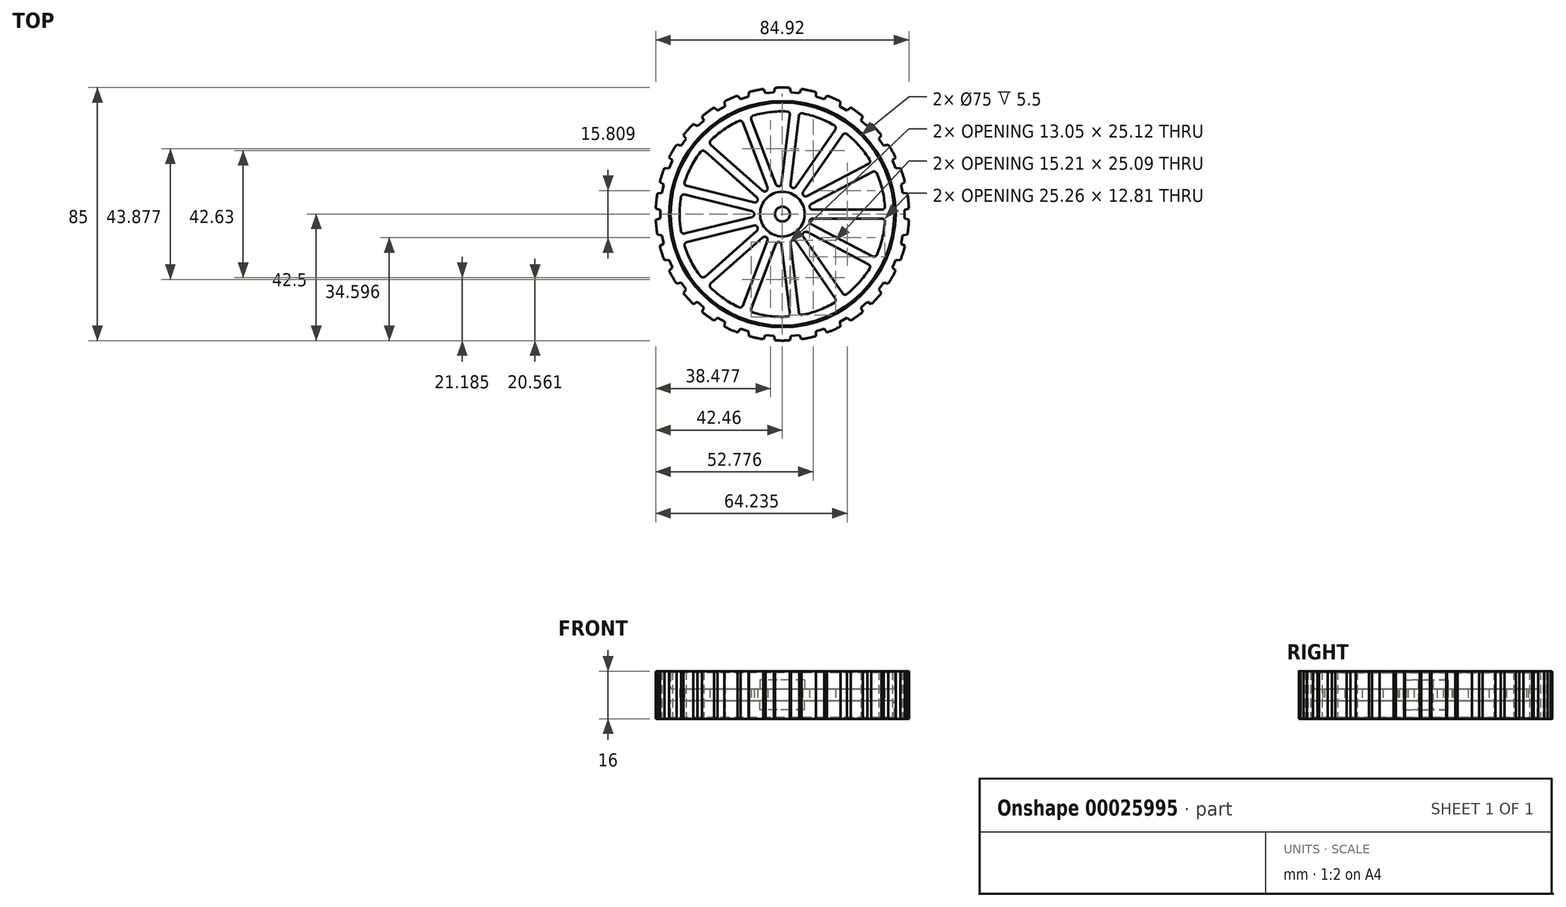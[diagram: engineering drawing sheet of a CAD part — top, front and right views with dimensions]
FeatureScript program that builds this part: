
annotation { "Feature Type Name" : "Feature", "Feature Type Description" : "" }
export const myFeature = defineFeature(function(context is Context, id is Id, definition is map)
    precondition{}
    {
        {
            var Q0;
            Q0=qCreatedBy(makeId("Top.planeOp"),FACE);
            var sketch = newSketch(context, id + "F0", { "sketchPlane" : qUnion([Q0])});
            skCircle(sketch, "E0.0", {"center": v(0, 0) * mm, "radius": 37.5 * mm});
            skCircle(sketch, "E1", {"center": v(0, 0) * mm, "radius": 2.5 * mm});
            skCircle(sketch, "E2.0", {"center": v(0, 0) * mm, "radius": 6.27 * mm, "construction": true});
            skLineSegment(sketch, "E3", {"start": v(-10.2, 0.97) * mm, "end": v(-32.8, 6.54) * mm});
            skLineSegment(sketch, "E4", {"start": v(-33.82, -6.8) * mm, "end": v(-33.82, -6.8) * mm});
            skLineSegment(sketch, "E5", {"start": v(0, 0) * mm, "end": v(-42.5, 0) * mm, "construction": true});
            skPoint(sketch, "E6.visualSharp", {"position": v(-6.27, 0) * mm});
            skArc(sketch, "E6.filletArc", {"start": v(-10.2, -0.97) * mm, "mid": v(-9.45, 0) * mm, "end": v(-10.2, 0.97) * mm});
            skLineSegment(sketch, "E7", {"start": v(-33.82, 6.8) * mm, "end": v(-33.82, 6.8) * mm});
            skLineSegment(sketch, "E8", {"start": v(-33.82, -6.8) * mm, "end": v(-32.8, -6.54) * mm, "construction": true});
            skCircle(sketch, "E9", {"center": v(0, 0) * mm, "radius": 7.5 * mm});
            skArc(sketch, "E10", {"start": v(-33.82, 6.8) * mm, "mid": v(-33.93, 6.26) * mm, "end": v(-34.02, 5.73) * mm, "construction": true});
            skLineSegment(sketch, "E11", {"start": v(-32.8, -6.54) * mm, "end": v(-10.2, -0.97) * mm});
            skArc(sketch, "E12", {"start": v(-34.02, -5.73) * mm, "mid": v(-33.93, -6.26) * mm, "end": v(-33.82, -6.8) * mm, "construction": true});
            skArc(sketch, "E13", {"start": v(-34.02, -5.73) * mm, "mid": v(-33.58, -6.4) * mm, "end": v(-32.8, -6.54) * mm});
            skArc(sketch, "E14", {"start": v(-32.8, -6.54) * mm, "mid": v(-32.49, -4.73) * mm, "end": v(-34.02, -5.73) * mm, "construction": true});
            skLineSegment(sketch, "E15", {"start": v(-32.8, 6.54) * mm, "end": v(-33.82, 6.8) * mm, "construction": true});
            skArc(sketch, "E16", {"start": v(-34.02, 5.73) * mm, "mid": v(-32.49, 4.73) * mm, "end": v(-32.8, 6.54) * mm, "construction": true});
            skArc(sketch, "E17", {"start": v(-32.8, 6.54) * mm, "mid": v(-33.58, 6.4) * mm, "end": v(-34.02, 5.73) * mm});
            skArc(sketch, "E18", {"start": v(-34.02, 5.73) * mm, "mid": v(-34.5, 0) * mm, "end": v(-34.02, -5.73) * mm});
            skLineSegment(sketch, "E19.1.0", {"start": v(-9.49, -3.88) * mm, "end": v(-32.08, -9.45) * mm});
            skArc(sketch, "E19.1.1", {"start": v(-32.08, -9.45) * mm, "mid": v(-32.71, -9.94) * mm, "end": v(-32.79, -10.73) * mm});
            skArc(sketch, "E19.1.2", {"start": v(-32.79, -10.73) * mm, "mid": v(-30.55, -16.03) * mm, "end": v(-27.46, -20.89) * mm});
            skArc(sketch, "E19.1.3", {"start": v(-27.46, -20.89) * mm, "mid": v(-26.76, -21.28) * mm, "end": v(-26, -21.03) * mm});
            skLineSegment(sketch, "E19.1.4", {"start": v(-26, -21.03) * mm, "end": v(-8.59, -5.6) * mm});
            skArc(sketch, "E19.1.5", {"start": v(-8.59, -5.6) * mm, "mid": v(-8.36, -4.39) * mm, "end": v(-9.49, -3.88) * mm});
            skLineSegment(sketch, "E19.2.0", {"start": v(-6.6, -7.85) * mm, "end": v(-24.01, -23.28) * mm});
            skArc(sketch, "E19.2.1", {"start": v(-24.01, -23.28) * mm, "mid": v(-24.35, -24) * mm, "end": v(-24.04, -24.74) * mm});
            skArc(sketch, "E19.2.2", {"start": v(-24.04, -24.74) * mm, "mid": v(-19.6, -28.4) * mm, "end": v(-14.6, -31.26) * mm});
            skArc(sketch, "E19.2.3", {"start": v(-14.6, -31.26) * mm, "mid": v(-13.8, -31.28) * mm, "end": v(-13.25, -30.7) * mm});
            skLineSegment(sketch, "E19.2.4", {"start": v(-13.25, -30.7) * mm, "end": v(-5, -8.95) * mm});
            skArc(sketch, "E19.2.5", {"start": v(-5, -8.95) * mm, "mid": v(-5.37, -7.77) * mm, "end": v(-6.6, -7.85) * mm});
            skLineSegment(sketch, "E20.2.3.0", {"start": v(-2.2, -10.02) * mm, "end": v(-10.44, -31.77) * mm});
            skArc(sketch, "E20.3.3.0", {"start": v(-10.44, -31.77) * mm, "mid": v(-10.4, -32.57) * mm, "end": v(-9.8, -33.08) * mm});
            skArc(sketch, "E20.7.3.0", {"start": v(-9.8, -33.08) * mm, "mid": v(-4.16, -34.25) * mm, "end": v(1.6, -34.46) * mm});
            skArc(sketch, "E20.11.3.0", {"start": v(1.6, -34.46) * mm, "mid": v(2.3, -34.11) * mm, "end": v(2.54, -33.34) * mm});
            skLineSegment(sketch, "E20.15.3.0", {"start": v(2.54, -33.34) * mm, "end": v(-0.27, -10.25) * mm});
            skArc(sketch, "E20.18.3.0", {"start": v(-0.27, -10.25) * mm, "mid": v(-1.14, -9.38) * mm, "end": v(-2.2, -10.02) * mm});
            skLineSegment(sketch, "E20.2.4.0", {"start": v(2.71, -9.89) * mm, "end": v(5.52, -32.98) * mm});
            skArc(sketch, "E20.3.4.0", {"start": v(5.52, -32.98) * mm, "mid": v(5.92, -33.67) * mm, "end": v(6.7, -33.84) * mm});
            skArc(sketch, "E20.7.4.0", {"start": v(6.7, -33.84) * mm, "mid": v(12.23, -32.26) * mm, "end": v(17.42, -29.78) * mm});
            skArc(sketch, "E20.11.4.0", {"start": v(17.42, -29.78) * mm, "mid": v(17.9, -29.13) * mm, "end": v(17.74, -28.35) * mm});
            skLineSegment(sketch, "E20.15.4.0", {"start": v(17.74, -28.35) * mm, "end": v(4.53, -9.2) * mm});
            skArc(sketch, "E20.18.4.0", {"start": v(4.53, -9.2) * mm, "mid": v(3.35, -8.83) * mm, "end": v(2.71, -9.89) * mm});
            skLineSegment(sketch, "E20.2.5.0", {"start": v(7, -7.5) * mm, "end": v(20.21, -26.64) * mm});
            skArc(sketch, "E20.3.5.0", {"start": v(20.21, -26.64) * mm, "mid": v(20.9, -27.06) * mm, "end": v(21.66, -26.85) * mm});
            skArc(sketch, "E20.7.5.0", {"start": v(21.66, -26.85) * mm, "mid": v(25.82, -22.88) * mm, "end": v(29.27, -18.27) * mm});
            skArc(sketch, "E20.11.5.0", {"start": v(29.27, -18.27) * mm, "mid": v(29.38, -17.48) * mm, "end": v(28.88, -16.85) * mm});
            skLineSegment(sketch, "E20.15.5.0", {"start": v(28.88, -16.85) * mm, "end": v(8.28, -6.04) * mm});
            skArc(sketch, "E20.18.5.0", {"start": v(8.28, -6.04) * mm, "mid": v(7.07, -6.26) * mm, "end": v(7, -7.5) * mm});
            skLineSegment(sketch, "E20.2.6.0", {"start": v(9.68, -3.39) * mm, "end": v(30.28, -14.2) * mm});
            skArc(sketch, "E20.3.6.0", {"start": v(30.28, -14.2) * mm, "mid": v(31.07, -14.25) * mm, "end": v(31.66, -13.7) * mm});
            skArc(sketch, "E20.7.6.0", {"start": v(31.66, -13.7) * mm, "mid": v(33.5, -8.26) * mm, "end": v(34.4, -2.57) * mm});
            skArc(sketch, "E20.11.6.0", {"start": v(34.4, -2.57) * mm, "mid": v(34.14, -1.82) * mm, "end": v(33.4, -1.5) * mm});
            skLineSegment(sketch, "E20.15.6.0", {"start": v(33.4, -1.5) * mm, "end": v(10.14, -1.5) * mm});
            skArc(sketch, "E20.18.6.0", {"start": v(10.14, -1.5) * mm, "mid": v(9.17, -2.26) * mm, "end": v(9.68, -3.39) * mm});
            skLineSegment(sketch, "E20.2.7.0", {"start": v(10.14, 1.5) * mm, "end": v(33.4, 1.5) * mm});
            skArc(sketch, "E20.3.7.0", {"start": v(33.4, 1.5) * mm, "mid": v(34.14, 1.82) * mm, "end": v(34.4, 2.57) * mm});
            skArc(sketch, "E20.7.7.0", {"start": v(34.4, 2.57) * mm, "mid": v(33.5, 8.26) * mm, "end": v(31.66, 13.7) * mm});
            skArc(sketch, "E20.11.7.0", {"start": v(31.66, 13.7) * mm, "mid": v(31.07, 14.25) * mm, "end": v(30.28, 14.2) * mm});
            skLineSegment(sketch, "E20.15.7.0", {"start": v(30.28, 14.2) * mm, "end": v(9.68, 3.39) * mm});
            skArc(sketch, "E20.18.7.0", {"start": v(9.68, 3.39) * mm, "mid": v(9.17, 2.26) * mm, "end": v(10.14, 1.5) * mm});
            skLineSegment(sketch, "E20.2.8.0", {"start": v(8.28, 6.04) * mm, "end": v(28.88, 16.85) * mm});
            skArc(sketch, "E20.3.8.0", {"start": v(28.88, 16.85) * mm, "mid": v(29.38, 17.48) * mm, "end": v(29.27, 18.27) * mm});
            skArc(sketch, "E20.7.8.0", {"start": v(29.27, 18.27) * mm, "mid": v(25.82, 22.88) * mm, "end": v(21.66, 26.85) * mm});
            skArc(sketch, "E20.11.8.0", {"start": v(21.66, 26.85) * mm, "mid": v(20.9, 27.06) * mm, "end": v(20.21, 26.64) * mm});
            skLineSegment(sketch, "E20.15.8.0", {"start": v(20.21, 26.64) * mm, "end": v(7, 7.5) * mm});
            skArc(sketch, "E20.18.8.0", {"start": v(7, 7.5) * mm, "mid": v(7.07, 6.26) * mm, "end": v(8.28, 6.04) * mm});
            skLineSegment(sketch, "E20.2.9.0", {"start": v(4.53, 9.2) * mm, "end": v(17.74, 28.35) * mm});
            skArc(sketch, "E20.3.9.0", {"start": v(17.74, 28.35) * mm, "mid": v(17.9, 29.13) * mm, "end": v(17.42, 29.78) * mm});
            skArc(sketch, "E20.7.9.0", {"start": v(17.42, 29.78) * mm, "mid": v(12.23, 32.26) * mm, "end": v(6.7, 33.84) * mm});
            skArc(sketch, "E20.11.9.0", {"start": v(6.7, 33.84) * mm, "mid": v(5.92, 33.67) * mm, "end": v(5.52, 32.98) * mm});
            skLineSegment(sketch, "E20.15.9.0", {"start": v(5.52, 32.98) * mm, "end": v(2.71, 9.89) * mm});
            skArc(sketch, "E20.18.9.0", {"start": v(2.71, 9.89) * mm, "mid": v(3.35, 8.83) * mm, "end": v(4.53, 9.2) * mm});
            skLineSegment(sketch, "E21.2.10.0", {"start": v(-0.27, 10.25) * mm, "end": v(2.54, 33.34) * mm});
            skArc(sketch, "E21.3.10.0", {"start": v(2.54, 33.34) * mm, "mid": v(2.3, 34.11) * mm, "end": v(1.6, 34.46) * mm});
            skArc(sketch, "E21.7.10.0", {"start": v(1.6, 34.46) * mm, "mid": v(-4.16, 34.25) * mm, "end": v(-9.8, 33.08) * mm});
            skArc(sketch, "E21.11.10.0", {"start": v(-9.8, 33.08) * mm, "mid": v(-10.4, 32.57) * mm, "end": v(-10.44, 31.77) * mm});
            skLineSegment(sketch, "E21.15.10.0", {"start": v(-10.44, 31.77) * mm, "end": v(-2.2, 10.02) * mm});
            skArc(sketch, "E21.18.10.0", {"start": v(-2.2, 10.02) * mm, "mid": v(-1.14, 9.38) * mm, "end": v(-0.27, 10.25) * mm});
            skLineSegment(sketch, "E21.2.11.0", {"start": v(-5, 8.95) * mm, "end": v(-13.25, 30.7) * mm});
            skArc(sketch, "E21.3.11.0", {"start": v(-13.25, 30.7) * mm, "mid": v(-13.8, 31.28) * mm, "end": v(-14.6, 31.26) * mm});
            skArc(sketch, "E21.7.11.0", {"start": v(-14.6, 31.26) * mm, "mid": v(-19.6, 28.4) * mm, "end": v(-24.04, 24.74) * mm});
            skArc(sketch, "E21.11.11.0", {"start": v(-24.04, 24.74) * mm, "mid": v(-24.35, 24) * mm, "end": v(-24.01, 23.28) * mm});
            skLineSegment(sketch, "E21.15.11.0", {"start": v(-24.01, 23.28) * mm, "end": v(-6.6, 7.85) * mm});
            skArc(sketch, "E21.18.11.0", {"start": v(-6.6, 7.85) * mm, "mid": v(-5.37, 7.77) * mm, "end": v(-5, 8.95) * mm});
            skLineSegment(sketch, "E21.2.12.0", {"start": v(-8.59, 5.6) * mm, "end": v(-26, 21.03) * mm});
            skArc(sketch, "E21.3.12.0", {"start": v(-26, 21.03) * mm, "mid": v(-26.76, 21.28) * mm, "end": v(-27.46, 20.89) * mm});
            skArc(sketch, "E21.7.12.0", {"start": v(-27.46, 20.89) * mm, "mid": v(-30.55, 16.03) * mm, "end": v(-32.79, 10.73) * mm});
            skArc(sketch, "E21.11.12.0", {"start": v(-32.79, 10.73) * mm, "mid": v(-32.71, 9.94) * mm, "end": v(-32.08, 9.45) * mm});
            skLineSegment(sketch, "E21.15.12.0", {"start": v(-32.08, 9.45) * mm, "end": v(-9.49, 3.88) * mm});
            skArc(sketch, "E21.18.12.0", {"start": v(-9.49, 3.88) * mm, "mid": v(-8.36, 4.39) * mm, "end": v(-8.59, 5.6) * mm});
            skLineSegment(sketch, "E22", {"start": v(-42.46, 1.95) * mm, "end": v(-41, 1.42) * mm});
            skLineSegment(sketch, "E23", {"start": v(-41, 1.42) * mm, "end": v(-41, -1.42) * mm});
            skLineSegment(sketch, "E24", {"start": v(-41, -1.42) * mm, "end": v(-42.46, -1.95) * mm});
            skArc(sketch, "E25", {"start": v(-41.93, 6.92) * mm, "mid": v(-42.27, 4.44) * mm, "end": v(-42.46, 1.95) * mm});
            skArc(sketch, "E26", {"start": v(-42.46, 1.95) * mm, "mid": v(-42.5, 0) * mm, "end": v(-42.46, -1.95) * mm, "construction": true});
            skLineSegment(sketch, "E27.1.0", {"start": v(-39.8, -9.91) * mm, "end": v(-41.12, -10.73) * mm});
            skLineSegment(sketch, "E27.1.1", {"start": v(-40.4, -7.14) * mm, "end": v(-39.8, -9.91) * mm});
            skLineSegment(sketch, "E27.1.2", {"start": v(-41.93, -6.92) * mm, "end": v(-40.4, -7.14) * mm});
            skArc(sketch, "E27.1.3", {"start": v(-42.46, -1.95) * mm, "mid": v(-42.27, -4.44) * mm, "end": v(-41.93, -6.92) * mm});
            skLineSegment(sketch, "E27.2.0", {"start": v(-36.88, -17.97) * mm, "end": v(-38, -19.05) * mm});
            skLineSegment(sketch, "E27.2.1", {"start": v(-38.03, -15.38) * mm, "end": v(-36.88, -17.97) * mm});
            skLineSegment(sketch, "E27.2.2", {"start": v(-39.58, -15.49) * mm, "end": v(-38.03, -15.38) * mm});
            skArc(sketch, "E27.2.3", {"start": v(-41.12, -10.73) * mm, "mid": v(-40.42, -13.13) * mm, "end": v(-39.58, -15.49) * mm});
            skLineSegment(sketch, "E27.3.0", {"start": v(-32.34, -25.25) * mm, "end": v(-33.2, -26.53) * mm});
            skLineSegment(sketch, "E27.3.1", {"start": v(-34, -22.95) * mm, "end": v(-32.34, -25.25) * mm});
            skLineSegment(sketch, "E27.3.2", {"start": v(-35.5, -23.38) * mm, "end": v(-34, -22.95) * mm});
            skArc(sketch, "E27.3.3", {"start": v(-38, -19.05) * mm, "mid": v(-36.8, -21.25) * mm, "end": v(-35.5, -23.38) * mm});
            skLineSegment(sketch, "E27.4.0", {"start": v(-26.38, -31.42) * mm, "end": v(-26.96, -32.85) * mm});
            skLineSegment(sketch, "E27.4.1", {"start": v(-28.49, -29.52) * mm, "end": v(-26.38, -31.42) * mm});
            skLineSegment(sketch, "E27.4.2", {"start": v(-29.86, -30.25) * mm, "end": v(-28.49, -29.52) * mm});
            skArc(sketch, "E27.4.3", {"start": v(-33.2, -26.53) * mm, "mid": v(-31.58, -28.44) * mm, "end": v(-29.86, -30.25) * mm});
            skLineSegment(sketch, "E27.5.0", {"start": v(-19.27, -36.22) * mm, "end": v(-19.54, -37.74) * mm});
            skLineSegment(sketch, "E27.5.1", {"start": v(-21.73, -34.8) * mm, "end": v(-19.27, -36.22) * mm});
            skLineSegment(sketch, "E27.5.2", {"start": v(-22.92, -35.8) * mm, "end": v(-21.73, -34.8) * mm});
            skArc(sketch, "E27.5.3", {"start": v(-26.96, -32.85) * mm, "mid": v(-24.98, -34.38) * mm, "end": v(-22.92, -35.8) * mm});
            skLineSegment(sketch, "E27.6.0", {"start": v(-11.32, -39.43) * mm, "end": v(-11.27, -40.98) * mm});
            skLineSegment(sketch, "E27.6.1", {"start": v(-14.02, -38.55) * mm, "end": v(-11.32, -39.43) * mm});
            skLineSegment(sketch, "E27.6.2", {"start": v(-14.97, -39.78) * mm, "end": v(-14.02, -38.55) * mm});
            skArc(sketch, "E27.6.3", {"start": v(-19.54, -37.74) * mm, "mid": v(-17.29, -38.83) * mm, "end": v(-14.97, -39.78) * mm});
            skLineSegment(sketch, "E27.7.0", {"start": v(-2.87, -40.92) * mm, "end": v(-2.5, -42.43) * mm});
            skLineSegment(sketch, "E27.7.1", {"start": v(-5.7, -40.63) * mm, "end": v(-2.87, -40.92) * mm});
            skLineSegment(sketch, "E27.7.2", {"start": v(-6.38, -42.02) * mm, "end": v(-5.7, -40.63) * mm});
            skArc(sketch, "E27.7.3", {"start": v(-11.27, -40.98) * mm, "mid": v(-8.84, -41.57) * mm, "end": v(-6.38, -42.02) * mm});
            skLineSegment(sketch, "E27.8.0", {"start": v(5.7, -40.63) * mm, "end": v(6.38, -42.02) * mm});
            skLineSegment(sketch, "E27.8.1", {"start": v(2.87, -40.92) * mm, "end": v(5.7, -40.63) * mm});
            skLineSegment(sketch, "E27.8.2", {"start": v(2.5, -42.43) * mm, "end": v(2.87, -40.92) * mm});
            skArc(sketch, "E27.8.3", {"start": v(-2.5, -42.43) * mm, "mid": v(0, -42.5) * mm, "end": v(2.5, -42.43) * mm});
            skLineSegment(sketch, "E27.9.0", {"start": v(14.02, -38.55) * mm, "end": v(14.97, -39.78) * mm});
            skLineSegment(sketch, "E27.9.1", {"start": v(11.32, -39.43) * mm, "end": v(14.02, -38.55) * mm});
            skLineSegment(sketch, "E27.9.2", {"start": v(11.27, -40.98) * mm, "end": v(11.32, -39.43) * mm});
            skArc(sketch, "E27.9.3", {"start": v(6.38, -42.02) * mm, "mid": v(8.84, -41.57) * mm, "end": v(11.27, -40.98) * mm});
            skLineSegment(sketch, "E28.2.10.0", {"start": v(21.73, -34.8) * mm, "end": v(22.92, -35.8) * mm});
            skLineSegment(sketch, "E28.3.10.0", {"start": v(19.27, -36.22) * mm, "end": v(21.73, -34.8) * mm});
            skLineSegment(sketch, "E28.6.10.0", {"start": v(19.54, -37.74) * mm, "end": v(19.27, -36.22) * mm});
            skArc(sketch, "E28.9.10.0", {"start": v(14.97, -39.78) * mm, "mid": v(17.29, -38.83) * mm, "end": v(19.54, -37.74) * mm});
            skLineSegment(sketch, "E28.2.11.0", {"start": v(28.49, -29.52) * mm, "end": v(29.86, -30.25) * mm});
            skLineSegment(sketch, "E28.3.11.0", {"start": v(26.38, -31.42) * mm, "end": v(28.49, -29.52) * mm});
            skLineSegment(sketch, "E28.6.11.0", {"start": v(26.96, -32.85) * mm, "end": v(26.38, -31.42) * mm});
            skArc(sketch, "E28.9.11.0", {"start": v(22.92, -35.8) * mm, "mid": v(24.98, -34.38) * mm, "end": v(26.96, -32.85) * mm});
            skLineSegment(sketch, "E28.2.12.0", {"start": v(34, -22.95) * mm, "end": v(35.5, -23.38) * mm});
            skLineSegment(sketch, "E28.3.12.0", {"start": v(32.34, -25.25) * mm, "end": v(34, -22.95) * mm});
            skLineSegment(sketch, "E28.6.12.0", {"start": v(33.2, -26.53) * mm, "end": v(32.34, -25.25) * mm});
            skArc(sketch, "E28.9.12.0", {"start": v(29.86, -30.25) * mm, "mid": v(31.58, -28.44) * mm, "end": v(33.2, -26.53) * mm});
            skLineSegment(sketch, "E28.2.13.0", {"start": v(38.03, -15.38) * mm, "end": v(39.58, -15.49) * mm});
            skLineSegment(sketch, "E28.3.13.0", {"start": v(36.88, -17.97) * mm, "end": v(38.03, -15.38) * mm});
            skLineSegment(sketch, "E28.6.13.0", {"start": v(38, -19.05) * mm, "end": v(36.88, -17.97) * mm});
            skArc(sketch, "E28.9.13.0", {"start": v(35.5, -23.38) * mm, "mid": v(36.8, -21.25) * mm, "end": v(38, -19.05) * mm});
            skLineSegment(sketch, "E28.2.14.0", {"start": v(40.4, -7.14) * mm, "end": v(41.93, -6.92) * mm});
            skLineSegment(sketch, "E28.3.14.0", {"start": v(39.8, -9.91) * mm, "end": v(40.4, -7.14) * mm});
            skLineSegment(sketch, "E28.6.14.0", {"start": v(41.12, -10.73) * mm, "end": v(39.8, -9.91) * mm});
            skArc(sketch, "E28.9.14.0", {"start": v(39.58, -15.49) * mm, "mid": v(40.42, -13.13) * mm, "end": v(41.12, -10.73) * mm});
            skLineSegment(sketch, "E28.2.15.0", {"start": v(41, 1.42) * mm, "end": v(42.46, 1.95) * mm});
            skLineSegment(sketch, "E28.3.15.0", {"start": v(41, -1.42) * mm, "end": v(41, 1.42) * mm});
            skLineSegment(sketch, "E28.6.15.0", {"start": v(42.46, -1.95) * mm, "end": v(41, -1.42) * mm});
            skArc(sketch, "E28.9.15.0", {"start": v(41.93, -6.92) * mm, "mid": v(42.27, -4.44) * mm, "end": v(42.46, -1.95) * mm});
            skLineSegment(sketch, "E28.2.16.0", {"start": v(39.8, 9.91) * mm, "end": v(41.12, 10.73) * mm});
            skLineSegment(sketch, "E28.3.16.0", {"start": v(40.4, 7.14) * mm, "end": v(39.8, 9.91) * mm});
            skLineSegment(sketch, "E28.6.16.0", {"start": v(41.93, 6.92) * mm, "end": v(40.4, 7.14) * mm});
            skArc(sketch, "E28.9.16.0", {"start": v(42.46, 1.95) * mm, "mid": v(42.27, 4.44) * mm, "end": v(41.93, 6.92) * mm});
            skLineSegment(sketch, "E28.2.17.0", {"start": v(36.88, 17.97) * mm, "end": v(38, 19.05) * mm});
            skLineSegment(sketch, "E28.3.17.0", {"start": v(38.03, 15.38) * mm, "end": v(36.88, 17.97) * mm});
            skLineSegment(sketch, "E28.6.17.0", {"start": v(39.58, 15.49) * mm, "end": v(38.03, 15.38) * mm});
            skArc(sketch, "E28.9.17.0", {"start": v(41.12, 10.73) * mm, "mid": v(40.42, 13.13) * mm, "end": v(39.58, 15.49) * mm});
            skLineSegment(sketch, "E28.2.18.0", {"start": v(32.34, 25.25) * mm, "end": v(33.2, 26.53) * mm});
            skLineSegment(sketch, "E28.3.18.0", {"start": v(34, 22.95) * mm, "end": v(32.34, 25.25) * mm});
            skLineSegment(sketch, "E28.6.18.0", {"start": v(35.5, 23.38) * mm, "end": v(34, 22.95) * mm});
            skArc(sketch, "E28.9.18.0", {"start": v(38, 19.05) * mm, "mid": v(36.8, 21.25) * mm, "end": v(35.5, 23.38) * mm});
            skLineSegment(sketch, "E28.2.19.0", {"start": v(26.38, 31.42) * mm, "end": v(26.96, 32.85) * mm});
            skLineSegment(sketch, "E28.3.19.0", {"start": v(28.49, 29.52) * mm, "end": v(26.38, 31.42) * mm});
            skLineSegment(sketch, "E28.6.19.0", {"start": v(29.86, 30.25) * mm, "end": v(28.49, 29.52) * mm});
            skArc(sketch, "E28.9.19.0", {"start": v(33.2, 26.53) * mm, "mid": v(31.58, 28.44) * mm, "end": v(29.86, 30.25) * mm});
            skLineSegment(sketch, "E29.2.20.0", {"start": v(19.27, 36.22) * mm, "end": v(19.54, 37.74) * mm});
            skLineSegment(sketch, "E29.3.20.0", {"start": v(21.73, 34.8) * mm, "end": v(19.27, 36.22) * mm});
            skLineSegment(sketch, "E29.6.20.0", {"start": v(22.92, 35.8) * mm, "end": v(21.73, 34.8) * mm});
            skArc(sketch, "E29.9.20.0", {"start": v(26.96, 32.85) * mm, "mid": v(24.98, 34.38) * mm, "end": v(22.92, 35.8) * mm});
            skLineSegment(sketch, "E29.2.21.0", {"start": v(11.32, 39.43) * mm, "end": v(11.27, 40.98) * mm});
            skLineSegment(sketch, "E29.3.21.0", {"start": v(14.02, 38.55) * mm, "end": v(11.32, 39.43) * mm});
            skLineSegment(sketch, "E29.6.21.0", {"start": v(14.97, 39.78) * mm, "end": v(14.02, 38.55) * mm});
            skArc(sketch, "E29.9.21.0", {"start": v(19.54, 37.74) * mm, "mid": v(17.29, 38.83) * mm, "end": v(14.97, 39.78) * mm});
            skLineSegment(sketch, "E29.2.22.0", {"start": v(2.87, 40.92) * mm, "end": v(2.5, 42.43) * mm});
            skLineSegment(sketch, "E29.3.22.0", {"start": v(5.7, 40.63) * mm, "end": v(2.87, 40.92) * mm});
            skLineSegment(sketch, "E29.6.22.0", {"start": v(6.38, 42.02) * mm, "end": v(5.7, 40.63) * mm});
            skArc(sketch, "E29.9.22.0", {"start": v(11.27, 40.98) * mm, "mid": v(8.84, 41.57) * mm, "end": v(6.38, 42.02) * mm});
            skLineSegment(sketch, "E29.2.23.0", {"start": v(-5.7, 40.63) * mm, "end": v(-6.38, 42.02) * mm});
            skLineSegment(sketch, "E29.3.23.0", {"start": v(-2.87, 40.92) * mm, "end": v(-5.7, 40.63) * mm});
            skLineSegment(sketch, "E29.6.23.0", {"start": v(-2.5, 42.43) * mm, "end": v(-2.87, 40.92) * mm});
            skArc(sketch, "E29.9.23.0", {"start": v(2.5, 42.43) * mm, "mid": v(0, 42.5) * mm, "end": v(-2.5, 42.43) * mm});
            skLineSegment(sketch, "E29.2.24.0", {"start": v(-14.02, 38.55) * mm, "end": v(-14.97, 39.78) * mm});
            skLineSegment(sketch, "E29.3.24.0", {"start": v(-11.32, 39.43) * mm, "end": v(-14.02, 38.55) * mm});
            skLineSegment(sketch, "E29.6.24.0", {"start": v(-11.27, 40.98) * mm, "end": v(-11.32, 39.43) * mm});
            skArc(sketch, "E29.9.24.0", {"start": v(-6.38, 42.02) * mm, "mid": v(-8.84, 41.57) * mm, "end": v(-11.27, 40.98) * mm});
            skLineSegment(sketch, "E29.2.25.0", {"start": v(-21.73, 34.8) * mm, "end": v(-22.92, 35.8) * mm});
            skLineSegment(sketch, "E29.3.25.0", {"start": v(-19.27, 36.22) * mm, "end": v(-21.73, 34.8) * mm});
            skLineSegment(sketch, "E29.6.25.0", {"start": v(-19.54, 37.74) * mm, "end": v(-19.27, 36.22) * mm});
            skArc(sketch, "E29.9.25.0", {"start": v(-14.97, 39.78) * mm, "mid": v(-17.29, 38.83) * mm, "end": v(-19.54, 37.74) * mm});
            skLineSegment(sketch, "E29.2.26.0", {"start": v(-28.49, 29.52) * mm, "end": v(-29.86, 30.25) * mm});
            skLineSegment(sketch, "E29.3.26.0", {"start": v(-26.38, 31.42) * mm, "end": v(-28.49, 29.52) * mm});
            skLineSegment(sketch, "E29.6.26.0", {"start": v(-26.96, 32.85) * mm, "end": v(-26.38, 31.42) * mm});
            skArc(sketch, "E29.9.26.0", {"start": v(-22.92, 35.8) * mm, "mid": v(-24.98, 34.38) * mm, "end": v(-26.96, 32.85) * mm});
            skLineSegment(sketch, "E29.2.27.0", {"start": v(-34, 22.95) * mm, "end": v(-35.5, 23.38) * mm});
            skLineSegment(sketch, "E29.3.27.0", {"start": v(-32.34, 25.25) * mm, "end": v(-34, 22.95) * mm});
            skLineSegment(sketch, "E29.6.27.0", {"start": v(-33.2, 26.53) * mm, "end": v(-32.34, 25.25) * mm});
            skArc(sketch, "E29.9.27.0", {"start": v(-29.86, 30.25) * mm, "mid": v(-31.58, 28.44) * mm, "end": v(-33.2, 26.53) * mm});
            skLineSegment(sketch, "E29.2.28.0", {"start": v(-38.03, 15.38) * mm, "end": v(-39.58, 15.49) * mm});
            skLineSegment(sketch, "E29.3.28.0", {"start": v(-36.88, 17.97) * mm, "end": v(-38.03, 15.38) * mm});
            skLineSegment(sketch, "E29.6.28.0", {"start": v(-38, 19.05) * mm, "end": v(-36.88, 17.97) * mm});
            skArc(sketch, "E29.9.28.0", {"start": v(-35.5, 23.38) * mm, "mid": v(-36.8, 21.25) * mm, "end": v(-38, 19.05) * mm});
            skLineSegment(sketch, "E29.2.29.0", {"start": v(-40.4, 7.14) * mm, "end": v(-41.93, 6.92) * mm});
            skLineSegment(sketch, "E29.3.29.0", {"start": v(-39.8, 9.91) * mm, "end": v(-40.4, 7.14) * mm});
            skLineSegment(sketch, "E29.6.29.0", {"start": v(-41.12, 10.73) * mm, "end": v(-39.8, 9.91) * mm});
            skArc(sketch, "E29.9.29.0", {"start": v(-39.58, 15.49) * mm, "mid": v(-40.42, 13.13) * mm, "end": v(-41.12, 10.73) * mm});
            skArc(sketch, "E30", {"start": v(-42.46, -1.95) * mm, "mid": v(42.43, -2.5) * mm, "end": v(-41.93, 6.92) * mm, "construction": true});
            skSolve(sketch);
        }
        {
            var Q0;
            {var subQ1=sQuery(id+"F0.wireOp",EDGE,"277decd8-61f1-49bf-b680-a9d94b4ffb41.9.0");Q0=makeQuery(id+"F0.imprint","IMPRINT",FACE,{"disambiguationData":[TD([[makeQuery(id+"F0.imprint","IMPRINT",EDGE,{"derivedFrom":subQ1}),1.0]])]});}
            var Q1;
            {var subQ1=sQuery(id+"F0.wireOp",EDGE,"277decd8-61f1-49bf-b680-a9d94b4ffb41.8.0");Q1=makeQuery(id+"F0.imprint","IMPRINT",FACE,{"disambiguationData":[TD([[makeQuery(id+"F0.imprint","IMPRINT",EDGE,{"derivedFrom":subQ1}),1.0]])]});}
            var Q2;
            {var subQ1=sQuery(id+"F0.wireOp",EDGE,"277decd8-61f1-49bf-b680-a9d94b4ffb41.7.0");Q2=makeQuery(id+"F0.imprint","IMPRINT",FACE,{"disambiguationData":[TD([[makeQuery(id+"F0.imprint","IMPRINT",EDGE,{"derivedFrom":subQ1}),1.0]])]});}
            var Q3;
            {var subQ1=sQuery(id+"F0.wireOp",EDGE,"277decd8-61f1-49bf-b680-a9d94b4ffb41.6.0");Q3=makeQuery(id+"F0.imprint","IMPRINT",FACE,{"disambiguationData":[TD([[makeQuery(id+"F0.imprint","IMPRINT",EDGE,{"derivedFrom":subQ1}),1.0]])]});}
            var Q4;
            {var subQ0=sQuery(id+"F0.wireOp",EDGE,"277decd8-61f1-49bf-b680-a9d94b4ffb41.5.0");Q4=makeQuery(id+"F0.imprint","IMPRINT",FACE,{"disambiguationData":[TD([[makeQuery(id+"F0.imprint","IMPRINT",EDGE,{"derivedFrom":subQ0}),1.0]])]});}
            var Q5;
            {var subQ1=sQuery(id+"F0.wireOp",EDGE,"277decd8-61f1-49bf-b680-a9d94b4ffb41.4.0");Q5=makeQuery(id+"F0.imprint","IMPRINT",FACE,{"disambiguationData":[TD([[makeQuery(id+"F0.imprint","IMPRINT",EDGE,{"derivedFrom":subQ1}),1.0]])]});}
            var Q6;
            {var subQ1=sQuery(id+"F0.wireOp",EDGE,"277decd8-61f1-49bf-b680-a9d94b4ffb41.3.0");Q6=makeQuery(id+"F0.imprint","IMPRINT",FACE,{"disambiguationData":[TD([[makeQuery(id+"F0.imprint","IMPRINT",EDGE,{"derivedFrom":subQ1}),1.0]])]});}
            var Q7;
            {var subQ1=sQuery(id+"F0.wireOp",EDGE,"277decd8-61f1-49bf-b680-a9d94b4ffb41.2.0");Q7=makeQuery(id+"F0.imprint","IMPRINT",FACE,{"disambiguationData":[TD([[makeQuery(id+"F0.imprint","IMPRINT",EDGE,{"derivedFrom":subQ1}),1.0]])]});}
            var Q8;
            {var subQ1=sQuery(id+"F0.wireOp",EDGE,"277decd8-61f1-49bf-b680-a9d94b4ffb41.1.0");Q8=makeQuery(id+"F0.imprint","IMPRINT",FACE,{"disambiguationData":[TD([[makeQuery(id+"F0.imprint","IMPRINT",EDGE,{"derivedFrom":subQ1}),1.0]])]});}
            var Q9;
            Q9=makeQuery(id+"F0.imprint","IMPRINT",FACE,{"disambiguationData":[TD([[makeQuery(id+"F0.imprint","IMPRINT",EDGE,{"derivedFrom":sQuery(id+"F0.wireOp",EDGE,"E0.0")}),1.0]])]});
            var Q10;
            {var subQ1=sQuery(id+"F0.wireOp",EDGE,"e2921473-2c19-45c7-b46e-fb2280c613b3.2.12.0");Q10=makeQuery(id+"F0.imprint","IMPRINT",FACE,{"disambiguationData":[TD([[makeQuery(id+"F0.imprint","IMPRINT",EDGE,{"derivedFrom":subQ1}),1.0]])]});}
            var Q11;
            {var subQ1=sQuery(id+"F0.wireOp",EDGE,"e2921473-2c19-45c7-b46e-fb2280c613b3.2.11.0");Q11=makeQuery(id+"F0.imprint","IMPRINT",FACE,{"disambiguationData":[TD([[makeQuery(id+"F0.imprint","IMPRINT",EDGE,{"derivedFrom":subQ1}),1.0]])]});}
            var Q12;
            {var subQ1=sQuery(id+"F0.wireOp",EDGE,"e2921473-2c19-45c7-b46e-fb2280c613b3.2.10.0");Q12=makeQuery(id+"F0.imprint","IMPRINT",FACE,{"disambiguationData":[TD([[makeQuery(id+"F0.imprint","IMPRINT",EDGE,{"derivedFrom":subQ1}),1.0]])]});}
            var Q13;
            Q13=makeQuery(id+"F0.imprint","IMPRINT",FACE,{"disambiguationData":[TD([[makeQuery(id+"F0.imprint","IMPRINT",EDGE,{"derivedFrom":sQuery(id+"F0.wireOp",EDGE,"E2.0")}),-1.0]])]});
            var Q14;
            {var subQ18=sQuery(id+"F0.wireOp",EDGE,"E3");Q14=makeQuery(id+"F0.imprint","IMPRINT",FACE,{"disambiguationData":[TD([[makeQuery(id+"F0.imprint","IMPRINT",EDGE,{"derivedFrom":subQ18}),-1.0]])]});}
            extrude(context, id + "F1", {"entities" : qUnion([Q0, Q1, Q2, Q3, Q4, Q5, Q6, Q7, Q8, Q9, Q10, Q11, Q12, Q13, Q14]), "depth" : 2 * mm});
        }
        {
            var Q0;
            Q0=makeQuery(id+"F0.imprint","IMPRINT",FACE,{"disambiguationData":[TD([[makeQuery(id+"F0.imprint","IMPRINT",EDGE,{"derivedFrom":sQuery(id+"F0.wireOp",EDGE,"E0.0")}),-1.0]])]});
            extrude(context, id + "F2", {"entities" : qUnion([Q0]), "operationType" : NewBodyOperationType.ADD, "depth" : 8 * mm});
        }
        {
            var Q0;
            Q0=makeQuery(id+"F0.imprint","IMPRINT",FACE,{"disambiguationData":[TD([[makeQuery(id+"F0.imprint","IMPRINT",EDGE,{"derivedFrom":sQuery(id+"F0.wireOp",EDGE,"E1")}),-1.0]])]});
            extrude(context, id + "F3", {"entities" : qUnion([Q0]), "operationType" : NewBodyOperationType.ADD, "depth" : 5 * mm});
        }
        {
            var Q0;
            Q0=makeQuery(id+"F2.opExtrude","CAP_EDGE",EDGE,{"disambiguationData":[OSD([sQuery(id+"F0.wireOp",EDGE,"E0.0")])],"isStart":false});
            chamfer(context, id + "F4", {"entities" : qUnion([Q0]), "width" : 0.5 * mm, "tangentPropagation" : true});
        }
        {
            var Q0;
            Q0=makeQuery(id+"F1.opExtrude","SWEPT_BODY",BODY,{"disambiguationData":[OSD([sQuery(id+"F0.wireOp",EDGE,"682aed11-c5d4-4406-a191-f2d0012fe9df"),sQuery(id+"F0.wireOp",EDGE,"E0.0"),sQuery(id+"F0.wireOp",EDGE,"E1"),sQuery(id+"F0.wireOp",EDGE,"E2.0"),sQuery(id+"F0.wireOp",EDGE,"E3"),sQuery(id+"F0.wireOp",EDGE,"E4"),sQuery(id+"F0.wireOp",EDGE,"277decd8-61f1-49bf-b680-a9d94b4ffb41.1.0"),sQuery(id+"F0.wireOp",EDGE,"277decd8-61f1-49bf-b680-a9d94b4ffb41.1.1"),sQuery(id+"F0.wireOp",EDGE,"277decd8-61f1-49bf-b680-a9d94b4ffb41.2.0"),sQuery(id+"F0.wireOp",EDGE,"277decd8-61f1-49bf-b680-a9d94b4ffb41.2.1"),sQuery(id+"F0.wireOp",EDGE,"277decd8-61f1-49bf-b680-a9d94b4ffb41.3.0"),sQuery(id+"F0.wireOp",EDGE,"277decd8-61f1-49bf-b680-a9d94b4ffb41.3.1"),sQuery(id+"F0.wireOp",EDGE,"277decd8-61f1-49bf-b680-a9d94b4ffb41.4.0"),sQuery(id+"F0.wireOp",EDGE,"277decd8-61f1-49bf-b680-a9d94b4ffb41.4.1"),sQuery(id+"F0.wireOp",EDGE,"277decd8-61f1-49bf-b680-a9d94b4ffb41.5.0"),sQuery(id+"F0.wireOp",EDGE,"277decd8-61f1-49bf-b680-a9d94b4ffb41.5.1"),sQuery(id+"F0.wireOp",EDGE,"277decd8-61f1-49bf-b680-a9d94b4ffb41.6.0"),sQuery(id+"F0.wireOp",EDGE,"277decd8-61f1-49bf-b680-a9d94b4ffb41.6.1"),sQuery(id+"F0.wireOp",EDGE,"277decd8-61f1-49bf-b680-a9d94b4ffb41.7.0"),sQuery(id+"F0.wireOp",EDGE,"277decd8-61f1-49bf-b680-a9d94b4ffb41.7.1"),sQuery(id+"F0.wireOp",EDGE,"277decd8-61f1-49bf-b680-a9d94b4ffb41.8.0"),sQuery(id+"F0.wireOp",EDGE,"277decd8-61f1-49bf-b680-a9d94b4ffb41.8.1"),sQuery(id+"F0.wireOp",EDGE,"277decd8-61f1-49bf-b680-a9d94b4ffb41.9.0"),sQuery(id+"F0.wireOp",EDGE,"277decd8-61f1-49bf-b680-a9d94b4ffb41.9.1")])]});
            var Q1;
            {var subQ0=sQuery(id+"F0.wireOp",EDGE,"E0.0");Q1=makeQuery(id+"F2.boolean.opBoolean","MERGE",FACE,{"derivedFrom":[makeQuery(id+"F1.opExtrude","CAP_FACE",FACE,{"disambiguationData":[OSD([sQuery(id+"F0.wireOp",EDGE,"682aed11-c5d4-4406-a191-f2d0012fe9df"),subQ0,sQuery(id+"F0.wireOp",EDGE,"E1"),sQuery(id+"F0.wireOp",EDGE,"E2.0"),sQuery(id+"F0.wireOp",EDGE,"E3"),sQuery(id+"F0.wireOp",EDGE,"E4"),sQuery(id+"F0.wireOp",EDGE,"277decd8-61f1-49bf-b680-a9d94b4ffb41.1.0"),sQuery(id+"F0.wireOp",EDGE,"277decd8-61f1-49bf-b680-a9d94b4ffb41.1.1"),sQuery(id+"F0.wireOp",EDGE,"277decd8-61f1-49bf-b680-a9d94b4ffb41.2.0"),sQuery(id+"F0.wireOp",EDGE,"277decd8-61f1-49bf-b680-a9d94b4ffb41.2.1"),sQuery(id+"F0.wireOp",EDGE,"277decd8-61f1-49bf-b680-a9d94b4ffb41.3.0"),sQuery(id+"F0.wireOp",EDGE,"277decd8-61f1-49bf-b680-a9d94b4ffb41.3.1"),sQuery(id+"F0.wireOp",EDGE,"277decd8-61f1-49bf-b680-a9d94b4ffb41.4.0"),sQuery(id+"F0.wireOp",EDGE,"277decd8-61f1-49bf-b680-a9d94b4ffb41.4.1"),sQuery(id+"F0.wireOp",EDGE,"277decd8-61f1-49bf-b680-a9d94b4ffb41.5.0"),sQuery(id+"F0.wireOp",EDGE,"277decd8-61f1-49bf-b680-a9d94b4ffb41.5.1"),sQuery(id+"F0.wireOp",EDGE,"277decd8-61f1-49bf-b680-a9d94b4ffb41.6.0"),sQuery(id+"F0.wireOp",EDGE,"277decd8-61f1-49bf-b680-a9d94b4ffb41.6.1"),sQuery(id+"F0.wireOp",EDGE,"277decd8-61f1-49bf-b680-a9d94b4ffb41.7.0"),sQuery(id+"F0.wireOp",EDGE,"277decd8-61f1-49bf-b680-a9d94b4ffb41.7.1"),sQuery(id+"F0.wireOp",EDGE,"277decd8-61f1-49bf-b680-a9d94b4ffb41.8.0"),sQuery(id+"F0.wireOp",EDGE,"277decd8-61f1-49bf-b680-a9d94b4ffb41.8.1"),sQuery(id+"F0.wireOp",EDGE,"277decd8-61f1-49bf-b680-a9d94b4ffb41.9.0"),sQuery(id+"F0.wireOp",EDGE,"277decd8-61f1-49bf-b680-a9d94b4ffb41.9.1")])],"isStart":true}),makeQuery(id+"F2.opExtrude","CAP_FACE",FACE,{"disambiguationData":[OSD([subQ0,sQuery(id+"F0.wireOp",EDGE,"d50da7c9-4a96-4c45-85ea-581115f5090f.0")])],"isStart":true})]});}
            mirror(context, id + "F5", {"operationType" : NewBodyOperationType.ADD, "entities" : qUnion([Q0]), "mirrorPlane" : qUnion([Q1])});
        }
    });
